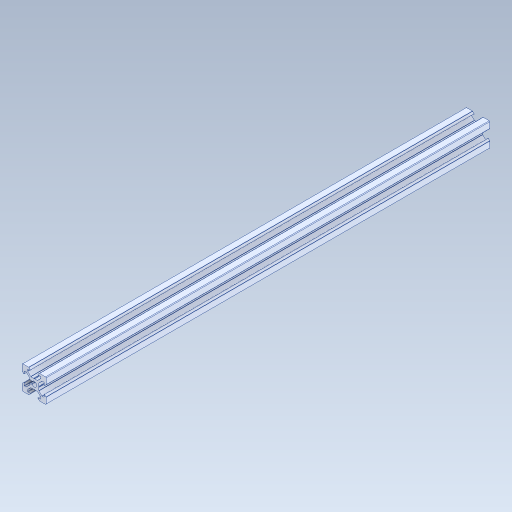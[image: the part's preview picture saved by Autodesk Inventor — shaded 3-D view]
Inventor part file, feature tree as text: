
AUTODESK INVENTOR PART (.ipt)
format: ipt  version: 2023 (Build 270158000, 158)  size: 364,032 bytes
history: mixed  units: in
note: dims shown in document units (in); Inventor stores cm internally (conversion verified against a paired STEP export)
features: other x3, extrude x1, sketch x1, projected_geometry x1, imported_body x1
ambient origin geometry x8: Origin, YZ Plane, XZ Plane, XY Plane, X Axis, Y Axis, Z Axis, Center Point
bodies: Solid1 (imported_parasolid)
feature tree (7):
  other  "Annotations"
  other  "Boss-Extrude1"
  extrude  "Extrusion1"  Depth=0.106in
  sketch  "Sketch2"  dims[d5=2.6772in d6=0.0in d0=0.106in d1=0.114in d2=17.3228in]
  projected_geometry  "Projected Loop1"
  other  "Linear Dimension 1"
  imported_body  NMx_Import_Brep_tag  [imported B-rep: ~114 faces, bbox_mm=[20.0, 20.0, 372.0]]
